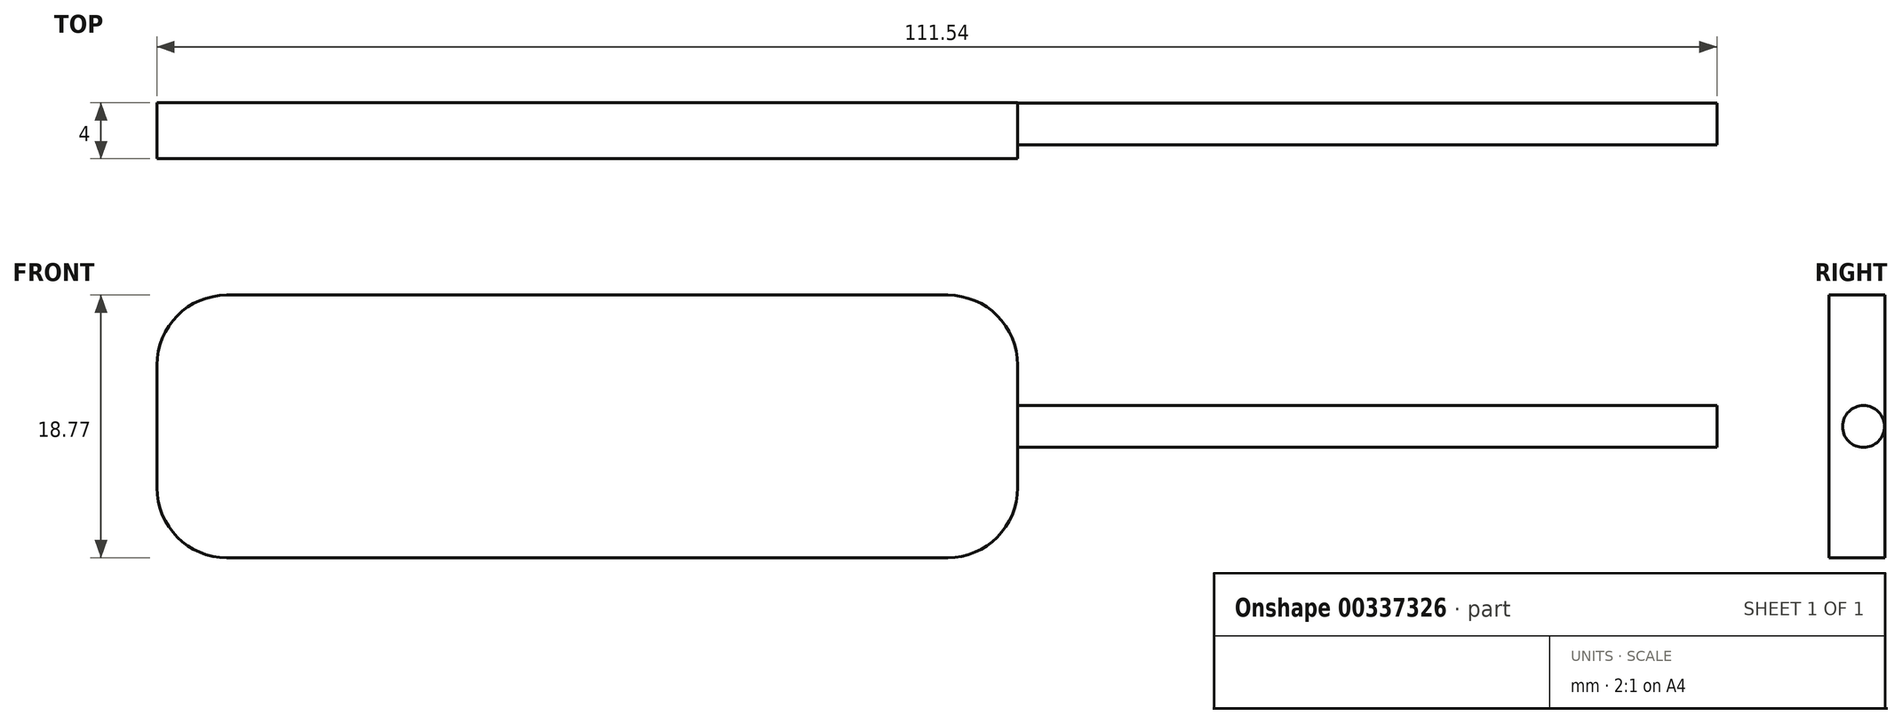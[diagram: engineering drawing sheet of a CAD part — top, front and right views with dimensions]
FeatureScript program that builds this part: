
annotation { "Feature Type Name" : "Feature", "Feature Type Description" : "" }
export const myFeature = defineFeature(function(context is Context, id is Id, definition is map)
    precondition{}
    {
        {
            var Q0;
            Q0=qCreatedBy(makeId("Front.planeOp"),FACE);
            var sketch = newSketch(context, id + "F0", { "sketchPlane" : qUnion([Q0])});
            skLineSegment(sketch, "E0.bottom", {"start": v(-28.38, 10.43) * mm, "end": v(23.16, 10.43) * mm});
            skLineSegment(sketch, "E0.top", {"start": v(-28.38, -8.34) * mm, "end": v(23.16, -8.34) * mm});
            skLineSegment(sketch, "E0.left", {"start": v(-33.38, 5.43) * mm, "end": v(-33.38, -3.34) * mm});
            skLineSegment(sketch, "E0.right", {"start": v(28.16, 5.43) * mm, "end": v(28.16, -3.34) * mm});
            skPoint(sketch, "E1.visualSharp", {"position": v(-33.38, 10.43) * mm});
            skArc(sketch, "E1.filletArc", {"start": v(-28.38, 10.43) * mm, "mid": v(-31.91, 8.97) * mm, "end": v(-33.38, 5.43) * mm});
            skPoint(sketch, "E2.visualSharp", {"position": v(-33.38, -8.34) * mm});
            skArc(sketch, "E2.filletArc", {"start": v(-33.38, -3.34) * mm, "mid": v(-31.91, -6.88) * mm, "end": v(-28.38, -8.34) * mm});
            skPoint(sketch, "E3.visualSharp", {"position": v(28.16, -8.34) * mm});
            skArc(sketch, "E3.filletArc", {"start": v(23.16, -8.34) * mm, "mid": v(26.7, -6.88) * mm, "end": v(28.16, -3.34) * mm});
            skPoint(sketch, "E4.visualSharp", {"position": v(28.16, 10.43) * mm});
            skArc(sketch, "E4.filletArc", {"start": v(28.16, 5.43) * mm, "mid": v(26.7, 8.97) * mm, "end": v(23.16, 10.43) * mm});
            skSolve(sketch);
        }
        {
            var Q0;
            Q0=makeQuery(id+"F0.imprint","IMPRINT",FACE,{"disambiguationData":[TD([[makeQuery(id+"F0.imprint","IMPRINT",EDGE,{"derivedFrom":sQuery(id+"F0.wireOp",EDGE,"E0.bottom")}),-1.0]])]});
            extrude(context, id + "F1", {"entities" : qUnion([Q0]), "depth" : 4 * mm});
        }
        {
            var Q0;
            Q0=makeQuery(id+"F1.opExtrude","SWEPT_FACE",FACE,{"disambiguationData":[OSD([sQuery(id+"F0.wireOp",EDGE,"E0.right")])]});
            var sketch = newSketch(context, id + "F2", { "sketchPlane" : qUnion([Q0])});
            skCircle(sketch, "E5", {"center": v(-1.52, 1.04) * mm, "radius": 1.5 * mm});
            skPoint(sketch, "E5.centerSnap0", {"position": v(-4, 1.04) * mm});
            skSolve(sketch);
        }
        {
            var Q0;
            Q0=makeQuery(id+"F2.imprint","IMPRINT",FACE,{"disambiguationData":[TD([[makeQuery(id+"F2.imprint","IMPRINT",EDGE,{"derivedFrom":sQuery(id+"F2.wireOp",EDGE,"E5")}),1.0]])]});
            extrude(context, id + "F3", {"entities" : qUnion([Q0]), "operationType" : NewBodyOperationType.ADD, "depth" : 50 * mm});
        }
    });
